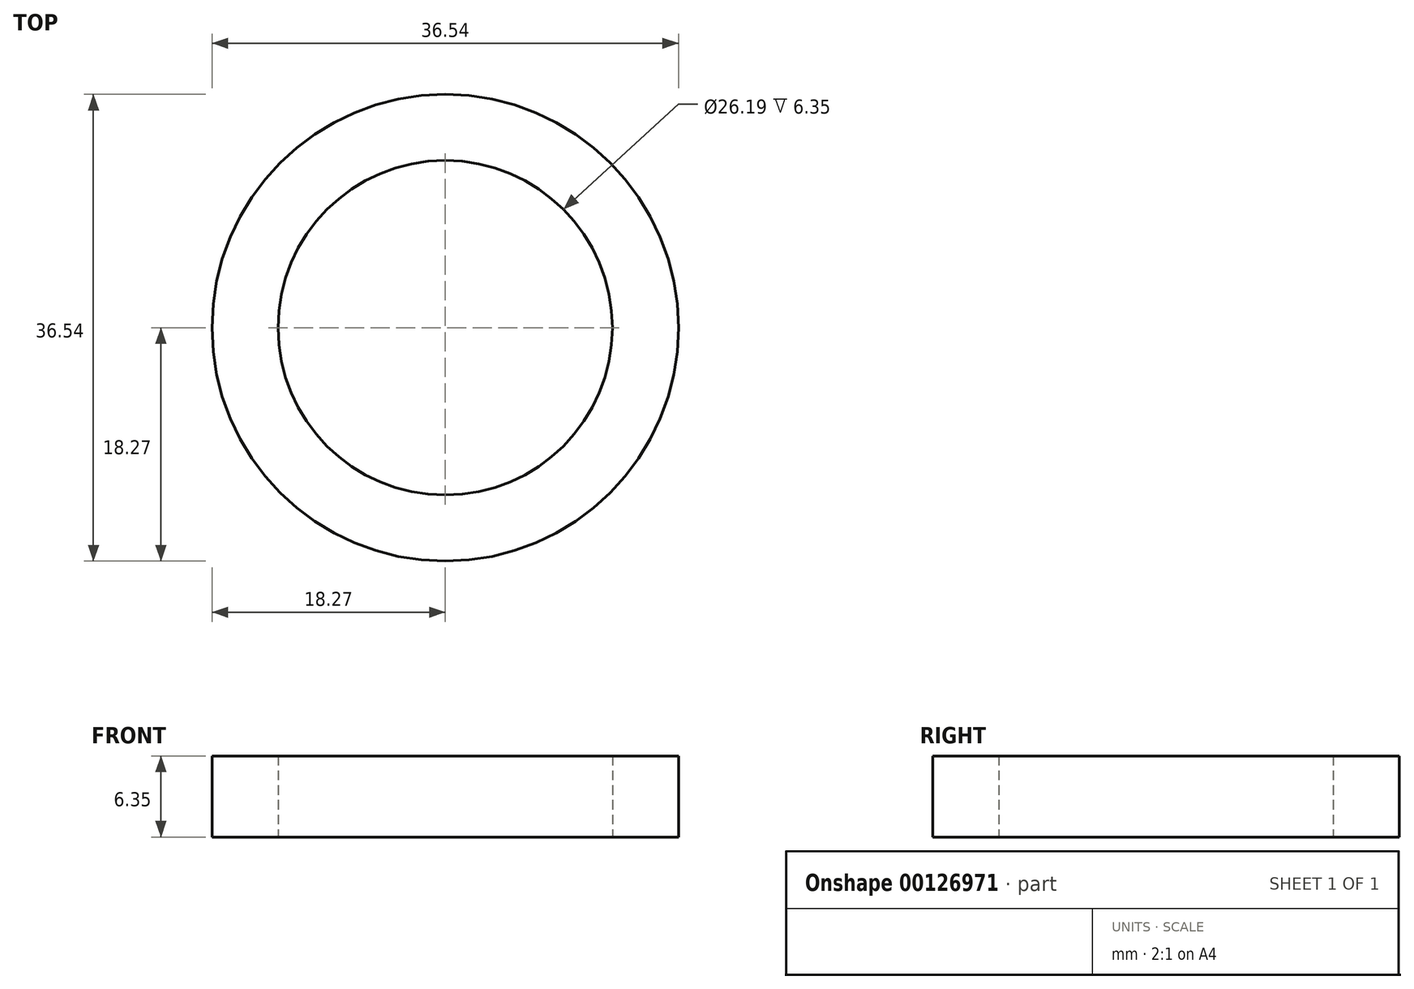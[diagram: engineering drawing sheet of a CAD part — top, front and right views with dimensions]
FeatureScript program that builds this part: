
annotation { "Feature Type Name" : "Feature", "Feature Type Description" : "" }
export const myFeature = defineFeature(function(context is Context, id is Id, definition is map)
    precondition{}
    {
        {
            var Q0;
            Q0=qCreatedBy(makeId("Top.planeOp"),FACE);
            var sketch = newSketch(context, id + "F0", { "sketchPlane" : qUnion([Q0])});
            skCircle(sketch, "E0", {"center": v(0, 0) * mm, "radius": 18.27 * mm});
            skSolve(sketch);
        }
        {
            var Q0;
            Q0=makeQuery(id+"F0.imprint","IMPRINT",FACE,{"disambiguationData":[TD([[makeQuery(id+"F0.imprint","IMPRINT",EDGE,{"derivedFrom":sQuery(id+"F0.wireOp",EDGE,"E0")}),1.0]])]});
            extrude(context, id + "F1", {"entities" : qUnion([Q0]), "depth" : 6.35 * mm});
        }
        {
            var Q0;
            Q0=sQuery(id+"F0.wireOp",VERTEX,"E0.center");
            var Q1;
            Q1=makeQuery(id+"F1.opExtrude","SWEPT_BODY",BODY,{"disambiguationData":[OSD([sQuery(id+"F0.wireOp",EDGE,"E0")])]});
            hole(context, id + "F2", {"style" : HoleStyle.SIMPLE, "endStyle" : HoleEndStyle.THROUGH, "oppositeDirection" : true, "holeDiameter" : 26.2 * mm, "locations" : qUnion([Q0]), "scope" : qUnion([Q1]), "tappedDepth" : 12.7 * mm, "tapClearance" : 3});
        }
    });
